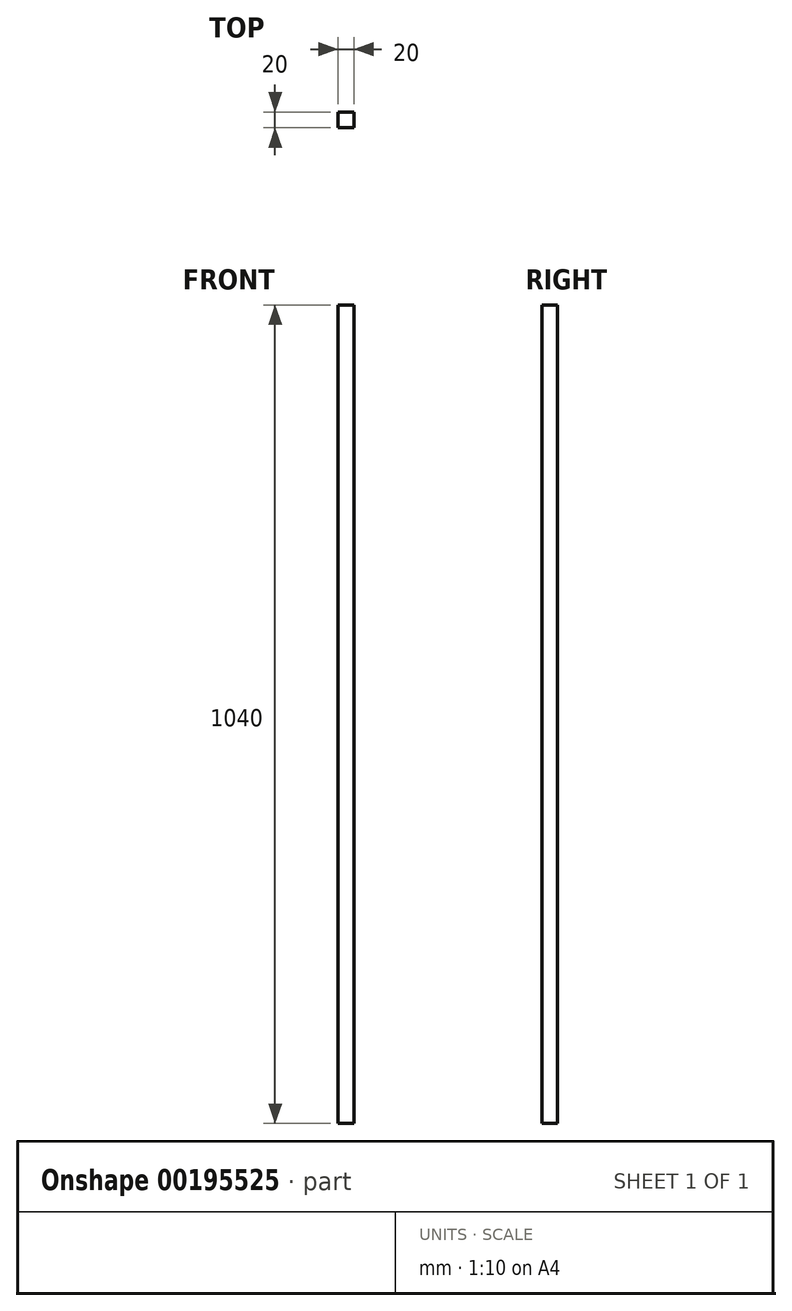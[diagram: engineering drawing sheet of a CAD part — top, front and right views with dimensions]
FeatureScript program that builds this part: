
annotation { "Feature Type Name" : "Feature", "Feature Type Description" : "" }
export const myFeature = defineFeature(function(context is Context, id is Id, definition is map)
    precondition{}
    {
        {
            var Q0;
            Q0=qCreatedBy(makeId("Top.planeOp"),FACE);
            var sketch = newSketch(context, id + "F0", { "sketchPlane" : qUnion([Q0])});
            skLineSegment(sketch, "E0.bottom", {"start": v(-91.8, -27.19) * mm, "end": v(-71.8, -27.19) * mm});
            skLineSegment(sketch, "E0.top", {"start": v(-91.8, -7.19) * mm, "end": v(-71.8, -7.19) * mm});
            skLineSegment(sketch, "E0.left", {"start": v(-91.8, -27.19) * mm, "end": v(-91.8, -7.19) * mm});
            skLineSegment(sketch, "E0.right", {"start": v(-71.8, -27.19) * mm, "end": v(-71.8, -7.19) * mm});
            skSolve(sketch);
        }
        {
            var Q0;
            Q0=makeQuery(id+"F0.imprint","IMPRINT",FACE,{"disambiguationData":[TD([[makeQuery(id+"F0.imprint","IMPRINT",EDGE,{"derivedFrom":sQuery(id+"F0.wireOp",EDGE,"E0.bottom")}),1.0]])]});
            extrude(context, id + "F1", {"entities" : qUnion([Q0]), "depth" : 1040 * mm});
        }
    });
